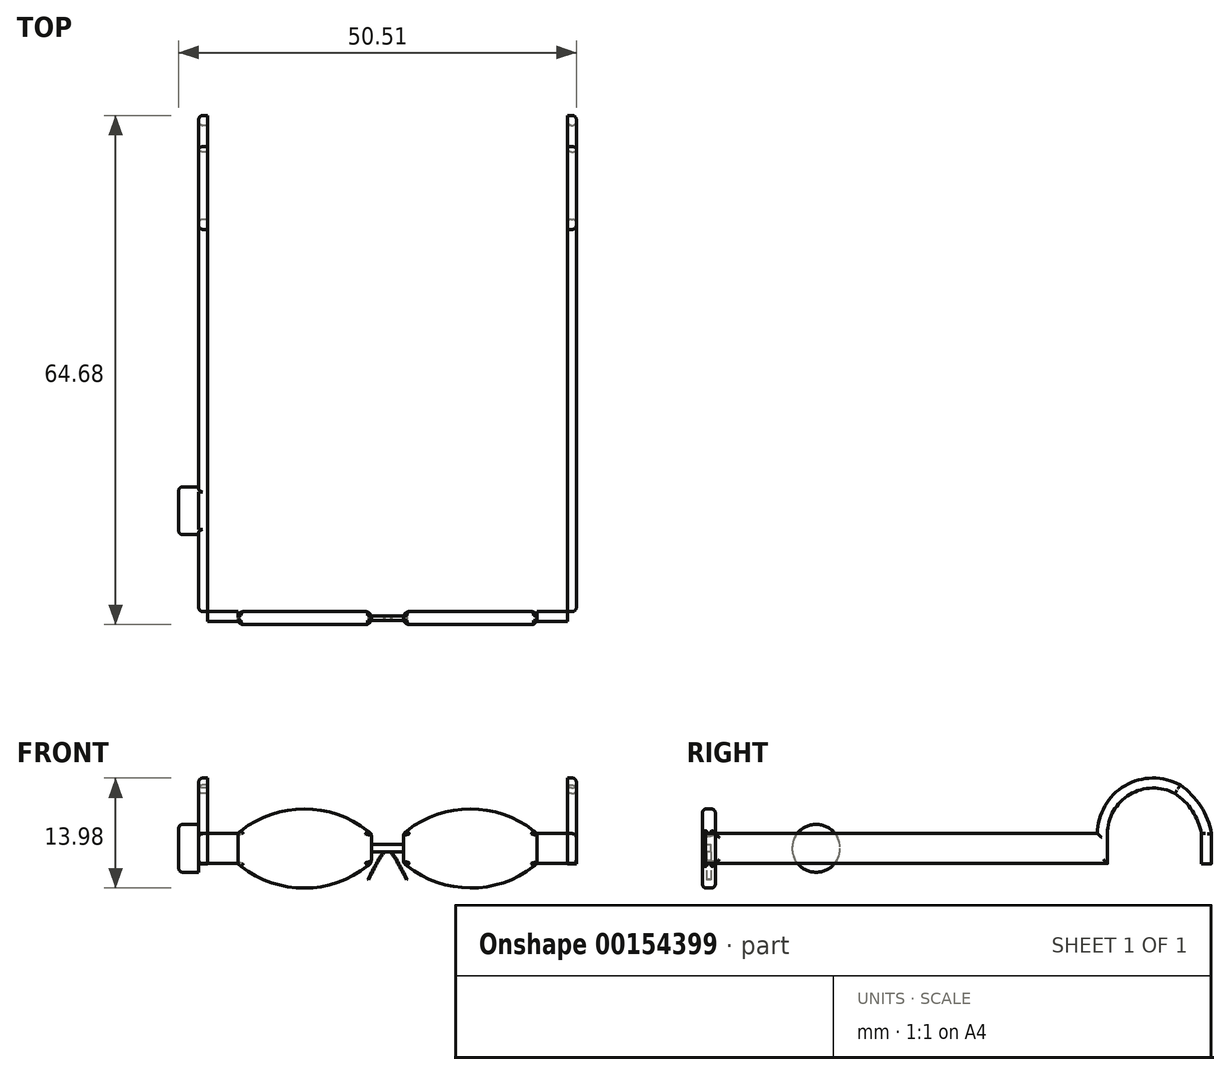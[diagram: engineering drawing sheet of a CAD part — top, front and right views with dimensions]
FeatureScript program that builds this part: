
annotation { "Feature Type Name" : "Feature", "Feature Type Description" : "" }
export const myFeature = defineFeature(function(context is Context, id is Id, definition is map)
    precondition{}
    {
        {
            var Q0;
            Q0=qCreatedBy(makeId("Right.planeOp"),FACE);
            var sketch = newSketch(context, id + "F0", { "sketchPlane" : qUnion([Q0])});
            skLineSegment(sketch, "E0.bottom", {"start": v(-42.94, 25.75) * mm, "end": v(5.61, 25.75) * mm});
            skLineSegment(sketch, "E0.top", {"start": v(-42.94, 21.94) * mm, "end": v(5.61, 21.94) * mm});
            skLineSegment(sketch, "E0.left", {"start": v(-42.94, 25.75) * mm, "end": v(-42.94, 21.94) * mm});
            skArc(sketch, "E1", {"start": v(16.12, 31.91) * mm, "mid": v(9.1, 31.84) * mm, "end": v(5.61, 25.75) * mm});
            skLineSegment(sketch, "E2", {"start": v(5.61, 21.94) * mm, "end": v(6.88, 21.94) * mm});
            skLineSegment(sketch, "E3", {"start": v(6.88, 21.94) * mm, "end": v(6.88, 25.75) * mm});
            skArc(sketch, "E4", {"start": v(15.45, 30.83) * mm, "mid": v(9.72, 30.73) * mm, "end": v(6.88, 25.75) * mm});
            skArc(sketch, "E5", {"start": v(20.09, 25.75) * mm, "mid": v(18.73, 29.23) * mm, "end": v(16.12, 31.91) * mm});
            skArc(sketch, "E6", {"start": v(18.82, 25.75) * mm, "mid": v(17.66, 28.64) * mm, "end": v(15.45, 30.83) * mm});
            skLineSegment(sketch, "E7", {"start": v(20.09, 25.75) * mm, "end": v(20.09, 21.93) * mm});
            skLineSegment(sketch, "E8", {"start": v(18.82, 25.75) * mm, "end": v(18.82, 21.94) * mm});
            skLineSegment(sketch, "E9", {"start": v(18.82, 21.94) * mm, "end": v(20.09, 21.93) * mm});
            skSolve(sketch);
        }
        {
            var Q0;
            Q0 = qSketchRegion(id + "F0", true);
            var Q1;
            Q1 = qConstructionFilter(qBodyType(qCreatedBy(id + "F0" ,EDGE), BodyType.WIRE), ConstructionObject.NO);
            extrude(context, id + "F1", {"entities" : qUnion([Q0]), "surfaceEntities" : qUnion([Q1]), "depth" : 1.14 * mm});
        }
        {
            var Q0;
            Q0=makeQuery(id+"F1.opExtrude","SWEPT_FACE",FACE,{"disambiguationData":[OSD([sQuery(id+"F0.wireOp",EDGE,"E0.left")])]});
            var sketch = newSketch(context, id + "F2", { "sketchPlane" : qUnion([Q0])});
            skLineSegment(sketch, "E10", {"start": v(4.93, 21.94) * mm, "end": v(4.93, 25.75) * mm});
            skLineSegment(sketch, "E11", {"start": v(21.93, 25.74) * mm, "end": v(21.93, 22) * mm});
            skLineSegment(sketch, "E12.MirrorCS", {"start": v(26, 25.75) * mm, "end": v(26, 22.02) * mm});
            skLineSegment(sketch, "E13.MirrorCS", {"start": v(43, 21.95) * mm, "end": v(43, 25.75) * mm});
            skLineSegment(sketch, "E14", {"start": v(46.79, 25.75) * mm, "end": v(46.79, 21.94) * mm});
            skLineSegment(sketch, "E15", {"start": v(1.14, 25.75) * mm, "end": v(1.14, 21.94) * mm});
            skArc(sketch, "E16", {"start": v(21.93, 25.74) * mm, "mid": v(13.43, 28.89) * mm, "end": v(4.93, 25.75) * mm});
            skArc(sketch, "E17", {"start": v(4.93, 21.94) * mm, "mid": v(13.44, 18.83) * mm, "end": v(21.93, 22) * mm});
            skArc(sketch, "E18", {"start": v(43, 25.75) * mm, "mid": v(34.5, 28.89) * mm, "end": v(26, 25.75) * mm});
            skArc(sketch, "E19", {"start": v(26, 22.02) * mm, "mid": v(34.5, 18.84) * mm, "end": v(43, 21.95) * mm});
            skLineSegment(sketch, "E20", {"start": v(4.93, 25.75) * mm, "end": v(1.14, 25.75) * mm});
            skLineSegment(sketch, "E21", {"start": v(43, 25.75) * mm, "end": v(46.79, 25.75) * mm});
            skLineSegment(sketch, "E22", {"start": v(26, 25.75) * mm, "end": v(43, 25.75) * mm});
            skLineSegment(sketch, "E23", {"start": v(21.93, 25.74) * mm, "end": v(4.93, 25.75) * mm});
            skLineSegment(sketch, "E24", {"start": v(26, 22.02) * mm, "end": v(43, 21.95) * mm});
            skSolve(sketch);
        }
        {
            var Q0;
            Q0 = qSketchRegion(id + "F2", true);
            extrude(context, id + "F3", {"entities" : qUnion([Q0]), "depth" : 1.65 * mm});
        }
        {
            var Q0;
            Q0=makeQuery(id+"F3.opExtrude","SWEPT_FACE",FACE,{"disambiguationData":[OSD([sQuery(id+"F2.wireOp",EDGE,"E12.MirrorCS")])]});
            var sketch = newSketch(context, id + "F4", { "sketchPlane" : qUnion([Q0])});
            skLineSegment(sketch, "E25.top", {"start": v(42.94, 25.75) * mm, "end": v(44.6, 25.75) * mm});
            skLineSegment(sketch, "E25.left", {"start": v(42.94, 25.75) * mm, "end": v(42.94, 25.75) * mm});
            skLineSegment(sketch, "E26.bottom", {"start": v(44.6, 22.02) * mm, "end": v(42.94, 22.02) * mm});
            skLineSegment(sketch, "E26.top", {"start": v(44.6, 25.75) * mm, "end": v(42.94, 25.75) * mm});
            skLineSegment(sketch, "E27", {"start": v(43.77, 25.75) * mm, "end": v(43.77, 22.02) * mm});
            skLineSegment(sketch, "E28", {"start": v(44.6, 23.88) * mm, "end": v(42.94, 23.88) * mm});
            skLineSegment(sketch, "E29.bottom", {"start": v(44.05, 23.4) * mm, "end": v(43.49, 23.4) * mm});
            skLineSegment(sketch, "E29.top", {"start": v(44.05, 24.36) * mm, "end": v(43.49, 24.36) * mm});
            skLineSegment(sketch, "E29.left", {"start": v(44.05, 23.4) * mm, "end": v(44.05, 24.36) * mm});
            skLineSegment(sketch, "E29.right", {"start": v(43.49, 23.4) * mm, "end": v(43.49, 24.36) * mm});
            skPoint(sketch, "E29.middle", {"position": v(43.77, 23.88) * mm});
            skSolve(sketch);
        }
        {
            var Q0;
            Q0 = qSketchRegion(id + "F4", true);
            extrude(context, id + "F5", {"entities" : qUnion([Q0]), "depth" : 4.13 * mm});
        }
        {
            var Q0;
            Q0=makeQuery(id+"F3.opExtrude","CAP_EDGE",EDGE,{"disambiguationData":[OSD([sQuery(id+"F2.wireOp",EDGE,"fc72fb57-17bc-4aef-a6e9-9f42b666f3fd4.MirrorCS")])],"isStart":false});
            var Q1;
            Q1=makeQuery(id+"F3.opExtrude","CAP_EDGE",EDGE,{"disambiguationData":[OSD([sQuery(id+"F2.wireOp",EDGE,"fc72fb57-17bc-4aef-a6e9-9f42b666f3fd4.MirrorCS")])],"isStart":true});
            var Q2;
            Q2=makeQuery(id+"F3.opExtrude","CAP_EDGE",EDGE,{"disambiguationData":[OSD([sQuery(id+"F2.wireOp",EDGE,"fc72fb57-17bc-4aef-a6e9-9f42b666f3fd3.MirrorCS")])],"isStart":false});
            var Q3;
            Q3=makeQuery(id+"F3.opExtrude","CAP_EDGE",EDGE,{"disambiguationData":[OSD([sQuery(id+"F2.wireOp",EDGE,"E12.MirrorCS")])],"isStart":false});
            var Q4;
            Q4=makeQuery(id+"F3.opExtrude","CAP_EDGE",EDGE,{"disambiguationData":[OSD([sQuery(id+"F2.wireOp",EDGE,"E12.MirrorCS")])],"isStart":true});
            var Q5;
            Q5=makeQuery(id+"F3.opExtrude","CAP_EDGE",EDGE,{"disambiguationData":[OSD([sQuery(id+"F2.wireOp",EDGE,"E13.MirrorCS")])],"isStart":false});
            var Q6;
            Q6=makeQuery(id+"F3.opExtrude","CAP_EDGE",EDGE,{"disambiguationData":[OSD([sQuery(id+"F2.wireOp",EDGE,"E13.MirrorCS")])],"isStart":true});
            var Q7;
            Q7=makeQuery(id+"F3.opExtrude","CAP_EDGE",EDGE,{"disambiguationData":[OSD([sQuery(id+"F2.wireOp",EDGE,"fc72fb57-17bc-4aef-a6e9-9f42b666f3fd3.MirrorCS")])],"isStart":true});
            var Q8;
            Q8=makeQuery(id+"F3.opExtrude","SWEPT_EDGE",EDGE,{"disambiguationData":[OSD([sQuery(id+"F2.wireOp",EDGE,"E12.MirrorCS"),sQuery(id+"F2.wireOp",EDGE,"fc72fb57-17bc-4aef-a6e9-9f42b666f3fd3.MirrorCS")])]});
            var Q9;
            Q9=makeQuery(id+"F3.opExtrude","SWEPT_EDGE",EDGE,{"disambiguationData":[OSD([sQuery(id+"F2.wireOp",EDGE,"E13.MirrorCS"),sQuery(id+"F2.wireOp",EDGE,"fc72fb57-17bc-4aef-a6e9-9f42b666f3fd3.MirrorCS")])]});
            var Q10;
            Q10=makeQuery(id+"F3.opExtrude","SWEPT_EDGE",EDGE,{"disambiguationData":[OSD([sQuery(id+"F2.wireOp",EDGE,"E13.MirrorCS"),sQuery(id+"F2.wireOp",EDGE,"fc72fb57-17bc-4aef-a6e9-9f42b666f3fd4.MirrorCS")])]});
            var Q11;
            Q11=makeQuery(id+"F3.opExtrude","CAP_EDGE",EDGE,{"disambiguationData":[OSD([sQuery(id+"F2.wireOp",EDGE,"E11")])],"isStart":true});
            var Q12;
            Q12=makeQuery(id+"F3.opExtrude","CAP_EDGE",EDGE,{"disambiguationData":[OSD([sQuery(id+"F2.wireOp",EDGE,"Gw3rG4JB-EbLj-57Wy-lnNk-VX72aqHDyFKe")])],"isStart":true});
            var Q13;
            Q13=makeQuery(id+"F3.opExtrude","CAP_EDGE",EDGE,{"disambiguationData":[OSD([sQuery(id+"F2.wireOp",EDGE,"E10")])],"isStart":true});
            var Q14;
            Q14=makeQuery(id+"F3.opExtrude","CAP_EDGE",EDGE,{"disambiguationData":[OSD([sQuery(id+"F2.wireOp",EDGE,"WBxUGhEL-5RnM-yJQJ-tIyO-uS8Gcnr4RgbC")])],"isStart":true});
            var Q15;
            Q15=makeQuery(id+"F3.opExtrude","CAP_EDGE",EDGE,{"disambiguationData":[OSD([sQuery(id+"F2.wireOp",EDGE,"Gw3rG4JB-EbLj-57Wy-lnNk-VX72aqHDyFKe")])],"isStart":false});
            var Q16;
            Q16=makeQuery(id+"F3.opExtrude","SWEPT_FACE",FACE,{"disambiguationData":[OSD([sQuery(id+"F2.wireOp",EDGE,"Gw3rG4JB-EbLj-57Wy-lnNk-VX72aqHDyFKe")])]});
            var Q17;
            Q17=makeQuery(id+"F3.opExtrude","CAP_EDGE",EDGE,{"disambiguationData":[OSD([sQuery(id+"F2.wireOp",EDGE,"E11")])],"isStart":false});
            var Q18;
            Q18=makeQuery(id+"F3.opExtrude","SWEPT_EDGE",EDGE,{"disambiguationData":[OSD([sQuery(id+"F2.wireOp",EDGE,"E11"),sQuery(id+"F2.wireOp",EDGE,"WBxUGhEL-5RnM-yJQJ-tIyO-uS8Gcnr4RgbC")])]});
            var Q19;
            Q19=makeQuery(id+"F3.opExtrude","CAP_EDGE",EDGE,{"disambiguationData":[OSD([sQuery(id+"F2.wireOp",EDGE,"E10")])],"isStart":false});
            var Q20;
            Q20=makeQuery(id+"F3.opExtrude","CAP_EDGE",EDGE,{"disambiguationData":[OSD([sQuery(id+"F2.wireOp",EDGE,"WBxUGhEL-5RnM-yJQJ-tIyO-uS8Gcnr4RgbC")])],"isStart":false});
            fillet(context, id + "F6", {"entities" : qUnion([Q0, Q1, Q2, Q3, Q4, Q5, Q6, Q7, Q8, Q9, Q10, Q11, Q12, Q13, Q14, Q15, Q16, Q17, Q18, Q19, Q20]), "radius" : 0.76 * mm, "tangentPropagation" : true, "allowEdgeOverflow" : false});
        }
        {
            var Q0;
            Q0=makeQuery(id+"F1.opExtrude","SWEPT_FACE",FACE,{"disambiguationData":[OSD([sQuery(id+"F0.wireOp",EDGE,"E0.left")])]});
            var sketch = newSketch(context, id + "F7", { "sketchPlane" : qUnion([Q0])});
            skLineSegment(sketch, "E30.bottom", {"start": v(1.14, 25.75) * mm, "end": v(5.01, 25.75) * mm});
            skLineSegment(sketch, "E30.top", {"start": v(1.14, 21.94) * mm, "end": v(5.01, 21.94) * mm});
            skLineSegment(sketch, "E30.left", {"start": v(1.14, 25.75) * mm, "end": v(1.14, 21.94) * mm});
            skLineSegment(sketch, "E30.right", {"start": v(5.01, 25.75) * mm, "end": v(5.01, 21.94) * mm});
            skSolve(sketch);
        }
        {
            var Q0;
            Q0=makeQuery(id+"F7.imprint","IMPRINT",FACE,{"disambiguationData":[TD([[makeQuery(id+"F7.imprint","IMPRINT",EDGE,{"derivedFrom":sQuery(id+"F7.wireOp",EDGE,"E30.bottom")}),-1.0]])]});
            extrude(context, id + "F8", {"entities" : qUnion([Q0]), "depth" : 1.27 * mm});
        }
        {
            var Q0;
            Q0=makeQuery(id+"F3.opExtrude","SWEPT_FACE",FACE,{"disambiguationData":[OSD([sQuery(id+"F2.wireOp",EDGE,"E11")])]});
            cPlane(context, id + "F9", {"entities" : qUnion([Q0]), "cplaneType" : CPlaneType.OFFSET, "offset" : 2.06 * mm, "width" : 152.4 * mm, "height" : 152.4 * mm});
        }
        {
            var Q0;
            Q0=makeQuery(id+"F1.opExtrude","SWEPT_BODY",BODY,{"disambiguationData":[OSD([sQuery(id+"F0.wireOp",EDGE,"E0.bottom"),sQuery(id+"F0.wireOp",EDGE,"E0.top"),sQuery(id+"F0.wireOp",EDGE,"E0.left"),sQuery(id+"F0.wireOp",EDGE,"E1"),sQuery(id+"F0.wireOp",EDGE,"E2"),sQuery(id+"F0.wireOp",EDGE,"E3"),sQuery(id+"F0.wireOp",EDGE,"E4"),sQuery(id+"F0.wireOp",EDGE,"E5"),sQuery(id+"F0.wireOp",EDGE,"E6"),sQuery(id+"F0.wireOp",EDGE,"E7"),sQuery(id+"F0.wireOp",EDGE,"E8"),sQuery(id+"F0.wireOp",EDGE,"E9")])]});
            var Q1;
            Q1=makeQuery(id+"F8.opExtrude","SWEPT_BODY",BODY,{"disambiguationData":[OSD([sQuery(id+"F7.wireOp",EDGE,"E30.bottom"),sQuery(id+"F7.wireOp",EDGE,"E30.top"),sQuery(id+"F7.wireOp",EDGE,"E30.left"),sQuery(id+"F7.wireOp",EDGE,"E30.right")])]});
            var Q2;
            Q2=qCreatedBy(id+"F9.planeOp",FACE);
            mirror(context, id + "F10", {"entities" : qUnion([Q0, Q1]), "mirrorPlane" : qUnion([Q2])});
        }
        {
            var Q0;
            Q0=makeQuery(id+"F1.opExtrude","CAP_FACE",FACE,{"disambiguationData":[OSD([sQuery(id+"F0.wireOp",EDGE,"E0.bottom"),sQuery(id+"F0.wireOp",EDGE,"E0.top"),sQuery(id+"F0.wireOp",EDGE,"E0.left"),sQuery(id+"F0.wireOp",EDGE,"E1"),sQuery(id+"F0.wireOp",EDGE,"E2"),sQuery(id+"F0.wireOp",EDGE,"E3"),sQuery(id+"F0.wireOp",EDGE,"E4"),sQuery(id+"F0.wireOp",EDGE,"E5"),sQuery(id+"F0.wireOp",EDGE,"E6"),sQuery(id+"F0.wireOp",EDGE,"E7"),sQuery(id+"F0.wireOp",EDGE,"E8"),sQuery(id+"F0.wireOp",EDGE,"E9")])],"isStart":true});
            var sketch = newSketch(context, id + "F11", { "sketchPlane" : qUnion([Q0])});
            skCircle(sketch, "E31", {"center": v(30.13, 23.89) * mm, "radius": 3.04 * mm});
            skSolve(sketch);
        }
        {
            var Q0;
            {var subQ0=sQuery(id+"F11.wireOp",EDGE,"E31");var subQ1=makeQuery(id+"F1.opExtrude","CAP_EDGE",EDGE,{"disambiguationData":[OSD([sQuery(id+"F0.wireOp",EDGE,"E0.top"),sQuery(id+"F0.wireOp",EDGE,"E2")])],"isStart":true});var subQ2=makeQuery(id+"F11.imprint","INTERSECT",VERTEX,{"disambiguationData":[OD(0.0)],"derivedFrom":[subQ1,subQ0]});Q0=makeQuery(id+"F11.imprint","IMPRINT",FACE,{"disambiguationData":[TD([[makeQuery(id+"F11.imprint","IMPRINT",EDGE,{"disambiguationData":[TD([[subQ2,-1.0]])],"derivedFrom":subQ0}),1.0]])]});}
            var Q1;
            {var subQ0=sQuery(id+"F11.wireOp",EDGE,"E31");var subQ1=makeQuery(id+"F1.opExtrude","CAP_EDGE",EDGE,{"disambiguationData":[OSD([sQuery(id+"F0.wireOp",EDGE,"E0.bottom")])],"isStart":true});var subQ2=makeQuery(id+"F11.imprint","INTERSECT",VERTEX,{"disambiguationData":[OD(0.0)],"derivedFrom":[subQ1,subQ0]});Q1=makeQuery(id+"F11.imprint","IMPRINT",FACE,{"disambiguationData":[TD([[makeQuery(id+"F11.imprint","IMPRINT",EDGE,{"disambiguationData":[TD([[subQ2,1.0]])],"derivedFrom":subQ1}),1.0]])]});}
            var Q2;
            {var subQ0=sQuery(id+"F11.wireOp",EDGE,"E31");var subQ1=makeQuery(id+"F1.opExtrude","CAP_EDGE",EDGE,{"disambiguationData":[OSD([sQuery(id+"F0.wireOp",EDGE,"E0.bottom")])],"isStart":true});var subQ2=makeQuery(id+"F11.imprint","INTERSECT",VERTEX,{"disambiguationData":[OD(0.0)],"derivedFrom":[subQ1,subQ0]});Q2=makeQuery(id+"F11.imprint","IMPRINT",FACE,{"disambiguationData":[TD([[makeQuery(id+"F11.imprint","IMPRINT",EDGE,{"disambiguationData":[TD([[subQ2,1.0]])],"derivedFrom":subQ0}),1.0]])]});}
            extrude(context, id + "F12", {"entities" : qUnion([Q0, Q1, Q2]), "operationType" : NewBodyOperationType.ADD, "depth" : 2.54 * mm});
        }
        {
            var Q0;
            Q0=makeQuery(id+"F12.opExtrude","CAP_EDGE",EDGE,{"disambiguationData":[OSD([sQuery(id+"F11.wireOp",EDGE,"E31")])],"isStart":false});
            var Q1;
            {var subQ0=sQuery(id+"F11.wireOp",EDGE,"E31");var subQ1=sQuery(id+"F0.wireOp",EDGE,"E1");var subQ2=sQuery(id+"F0.wireOp",EDGE,"E0.bottom");Q1=makeQuery(id+"F12.boolean.opBoolean","SPLIT",EDGE,{"disambiguationData":[TD([makeQuery(id+"F1.opExtrude","SWEPT_FACE",FACE,{"disambiguationData":[OSD([subQ2])]}),makeQuery(id+"F1.opExtrude","CAP_FACE",FACE,{"disambiguationData":[OSD([subQ2,sQuery(id+"F0.wireOp",EDGE,"E0.top"),sQuery(id+"F0.wireOp",EDGE,"E0.left"),subQ1,sQuery(id+"F0.wireOp",EDGE,"E2"),sQuery(id+"F0.wireOp",EDGE,"E3"),sQuery(id+"F0.wireOp",EDGE,"E4"),sQuery(id+"F0.wireOp",EDGE,"E5"),sQuery(id+"F0.wireOp",EDGE,"E6"),sQuery(id+"F0.wireOp",EDGE,"E7"),sQuery(id+"F0.wireOp",EDGE,"E8"),sQuery(id+"F0.wireOp",EDGE,"E9")])],"isStart":true}),makeQuery(id+"F1.opExtrude","SWEPT_FACE",FACE,{"disambiguationData":[OSD([subQ1])]}),makeQuery(id+"F12.opExtrude","SWEPT_FACE",FACE,{"disambiguationData":[OSD([subQ0])]}),makeQuery(id+"F12.opExtrude","CAP_FACE",FACE,{"disambiguationData":[OSD([subQ0])],"isStart":true})])],"derivedFrom":makeQuery(id+"F1.opExtrude","CAP_EDGE",EDGE,{"disambiguationData":[OSD([subQ2])],"isStart":true})});}
            var Q2;
            {var subQ0=sQuery(id+"F11.wireOp",EDGE,"E31");var subQ1=sQuery(id+"F0.wireOp",EDGE,"E0.left");var subQ2=sQuery(id+"F0.wireOp",EDGE,"E0.bottom");Q2=makeQuery(id+"F12.boolean.opBoolean","SPLIT",EDGE,{"disambiguationData":[TD([makeQuery(id+"F1.opExtrude","SWEPT_FACE",FACE,{"disambiguationData":[OSD([subQ2])]}),makeQuery(id+"F1.opExtrude","CAP_FACE",FACE,{"disambiguationData":[OSD([subQ2,sQuery(id+"F0.wireOp",EDGE,"E0.top"),subQ1,sQuery(id+"F0.wireOp",EDGE,"E1"),sQuery(id+"F0.wireOp",EDGE,"E2"),sQuery(id+"F0.wireOp",EDGE,"E3"),sQuery(id+"F0.wireOp",EDGE,"E4"),sQuery(id+"F0.wireOp",EDGE,"E5"),sQuery(id+"F0.wireOp",EDGE,"E6"),sQuery(id+"F0.wireOp",EDGE,"E7"),sQuery(id+"F0.wireOp",EDGE,"E8"),sQuery(id+"F0.wireOp",EDGE,"E9")])],"isStart":true}),makeQuery(id+"F1.opExtrude","SWEPT_FACE",FACE,{"disambiguationData":[OSD([subQ1])]}),makeQuery(id+"F12.opExtrude","SWEPT_FACE",FACE,{"disambiguationData":[OSD([subQ0])]}),makeQuery(id+"F12.opExtrude","CAP_FACE",FACE,{"disambiguationData":[OSD([subQ0])],"isStart":true})])],"derivedFrom":makeQuery(id+"F1.opExtrude","CAP_EDGE",EDGE,{"disambiguationData":[OSD([subQ2])],"isStart":true})});}
            var Q3;
            Q3=makeQuery(id+"F1.opExtrude","CAP_EDGE",EDGE,{"disambiguationData":[OSD([sQuery(id+"F0.wireOp",EDGE,"E0.left")])],"isStart":true});
            var Q4;
            {var subQ0=sQuery(id+"F0.wireOp",EDGE,"E3");var subQ1=sQuery(id+"F11.wireOp",EDGE,"E31");var subQ2=sQuery(id+"F0.wireOp",EDGE,"E2");var subQ3=sQuery(id+"F0.wireOp",EDGE,"E0.top");Q4=makeQuery(id+"F12.boolean.opBoolean","SPLIT",EDGE,{"disambiguationData":[TD([makeQuery(id+"F1.opExtrude","CAP_FACE",FACE,{"disambiguationData":[OSD([sQuery(id+"F0.wireOp",EDGE,"E0.bottom"),subQ3,sQuery(id+"F0.wireOp",EDGE,"E0.left"),sQuery(id+"F0.wireOp",EDGE,"E1"),subQ2,subQ0,sQuery(id+"F0.wireOp",EDGE,"E4"),sQuery(id+"F0.wireOp",EDGE,"E5"),sQuery(id+"F0.wireOp",EDGE,"E6"),sQuery(id+"F0.wireOp",EDGE,"E7"),sQuery(id+"F0.wireOp",EDGE,"E8"),sQuery(id+"F0.wireOp",EDGE,"E9")])],"isStart":true}),makeQuery(id+"F1.opExtrude","SWEPT_FACE",FACE,{"disambiguationData":[OSD([subQ3,subQ2])]}),makeQuery(id+"F1.opExtrude","SWEPT_FACE",FACE,{"disambiguationData":[OSD([subQ0])]}),makeQuery(id+"F12.opExtrude","SWEPT_FACE",FACE,{"disambiguationData":[OSD([subQ1])]}),makeQuery(id+"F12.opExtrude","CAP_FACE",FACE,{"disambiguationData":[OSD([subQ1])],"isStart":true})])],"derivedFrom":makeQuery(id+"F1.opExtrude","CAP_EDGE",EDGE,{"disambiguationData":[OSD([subQ3,subQ2])],"isStart":true})});}
            var Q5;
            {var subQ0=sQuery(id+"F0.wireOp",EDGE,"E0.left");var subQ1=sQuery(id+"F11.wireOp",EDGE,"E31");var subQ2=sQuery(id+"F0.wireOp",EDGE,"E2");var subQ3=sQuery(id+"F0.wireOp",EDGE,"E0.top");Q5=makeQuery(id+"F12.boolean.opBoolean","SPLIT",EDGE,{"disambiguationData":[TD([makeQuery(id+"F1.opExtrude","CAP_FACE",FACE,{"disambiguationData":[OSD([sQuery(id+"F0.wireOp",EDGE,"E0.bottom"),subQ3,subQ0,sQuery(id+"F0.wireOp",EDGE,"E1"),subQ2,sQuery(id+"F0.wireOp",EDGE,"E3"),sQuery(id+"F0.wireOp",EDGE,"E4"),sQuery(id+"F0.wireOp",EDGE,"E5"),sQuery(id+"F0.wireOp",EDGE,"E6"),sQuery(id+"F0.wireOp",EDGE,"E7"),sQuery(id+"F0.wireOp",EDGE,"E8"),sQuery(id+"F0.wireOp",EDGE,"E9")])],"isStart":true}),makeQuery(id+"F1.opExtrude","SWEPT_FACE",FACE,{"disambiguationData":[OSD([subQ3,subQ2])]}),makeQuery(id+"F1.opExtrude","SWEPT_FACE",FACE,{"disambiguationData":[OSD([subQ0])]}),makeQuery(id+"F12.opExtrude","SWEPT_FACE",FACE,{"disambiguationData":[OSD([subQ1])]}),makeQuery(id+"F12.opExtrude","CAP_FACE",FACE,{"disambiguationData":[OSD([subQ1])],"isStart":true})])],"derivedFrom":makeQuery(id+"F1.opExtrude","CAP_EDGE",EDGE,{"disambiguationData":[OSD([subQ3,subQ2])],"isStart":true})});}
            var Q6;
            Q6=makeQuery(id+"F1.opExtrude","CAP_EDGE",EDGE,{"disambiguationData":[OSD([sQuery(id+"F0.wireOp",EDGE,"E3")])],"isStart":true});
            var Q7;
            Q7=makeQuery(id+"F1.opExtrude","CAP_EDGE",EDGE,{"disambiguationData":[OSD([sQuery(id+"F0.wireOp",EDGE,"E6")])],"isStart":true});
            var Q8;
            Q8=makeQuery(id+"F1.opExtrude","CAP_EDGE",EDGE,{"disambiguationData":[OSD([sQuery(id+"F0.wireOp",EDGE,"E8")])],"isStart":true});
            var Q9;
            Q9=makeQuery(id+"F1.opExtrude","CAP_EDGE",EDGE,{"disambiguationData":[OSD([sQuery(id+"F0.wireOp",EDGE,"E7")])],"isStart":true});
            var Q10;
            Q10=makeQuery(id+"F1.opExtrude","CAP_EDGE",EDGE,{"disambiguationData":[OSD([sQuery(id+"F0.wireOp",EDGE,"E5")])],"isStart":true});
            var Q11;
            Q11=makeQuery(id+"F1.opExtrude","CAP_EDGE",EDGE,{"disambiguationData":[OSD([sQuery(id+"F0.wireOp",EDGE,"E1")])],"isStart":true});
            var Q12;
            Q12=makeQuery(id+"F1.opExtrude","CAP_EDGE",EDGE,{"disambiguationData":[OSD([sQuery(id+"F0.wireOp",EDGE,"E4")])],"isStart":true});
            var Q13;
            Q13=makeQuery(id+"F10.opPattern","COPY",EDGE,{"derivedFrom":makeQuery(id+"F1.opExtrude","CAP_EDGE",EDGE,{"disambiguationData":[OSD([sQuery(id+"F0.wireOp",EDGE,"E0.bottom")])],"isStart":true}),"instanceName":"1"});
            var Q14;
            Q14=makeQuery(id+"F10.opPattern","COPY",EDGE,{"derivedFrom":makeQuery(id+"F1.opExtrude","CAP_EDGE",EDGE,{"disambiguationData":[OSD([sQuery(id+"F0.wireOp",EDGE,"E0.top"),sQuery(id+"F0.wireOp",EDGE,"E2")])],"isStart":true}),"instanceName":"1"});
            var Q15;
            Q15=makeQuery(id+"F10.opPattern","COPY",EDGE,{"derivedFrom":makeQuery(id+"F1.opExtrude","CAP_EDGE",EDGE,{"disambiguationData":[OSD([sQuery(id+"F0.wireOp",EDGE,"E0.left")])],"isStart":true}),"instanceName":"1"});
            var Q16;
            Q16=makeQuery(id+"F10.opPattern","COPY",EDGE,{"derivedFrom":makeQuery(id+"F1.opExtrude","CAP_EDGE",EDGE,{"disambiguationData":[OSD([sQuery(id+"F0.wireOp",EDGE,"E3")])],"isStart":true}),"instanceName":"1"});
            var Q17;
            Q17=makeQuery(id+"F10.opPattern","COPY",EDGE,{"derivedFrom":makeQuery(id+"F1.opExtrude","CAP_EDGE",EDGE,{"disambiguationData":[OSD([sQuery(id+"F0.wireOp",EDGE,"E6")])],"isStart":true}),"instanceName":"1"});
            var Q18;
            Q18=makeQuery(id+"F10.opPattern","COPY",EDGE,{"derivedFrom":makeQuery(id+"F1.opExtrude","CAP_EDGE",EDGE,{"disambiguationData":[OSD([sQuery(id+"F0.wireOp",EDGE,"E6")])],"isStart":false}),"instanceName":"1"});
            var Q19;
            Q19=makeQuery(id+"F10.opPattern","COPY",EDGE,{"derivedFrom":makeQuery(id+"F1.opExtrude","CAP_EDGE",EDGE,{"disambiguationData":[OSD([sQuery(id+"F0.wireOp",EDGE,"E8")])],"isStart":true}),"instanceName":"1"});
            var Q20;
            Q20=makeQuery(id+"F10.opPattern","COPY",EDGE,{"derivedFrom":makeQuery(id+"F1.opExtrude","CAP_EDGE",EDGE,{"disambiguationData":[OSD([sQuery(id+"F0.wireOp",EDGE,"E7")])],"isStart":true}),"instanceName":"1"});
            var Q21;
            Q21=makeQuery(id+"F10.opPattern","COPY",EDGE,{"derivedFrom":makeQuery(id+"F1.opExtrude","CAP_EDGE",EDGE,{"disambiguationData":[OSD([sQuery(id+"F0.wireOp",EDGE,"E5")])],"isStart":true}),"instanceName":"1"});
            var Q22;
            Q22=makeQuery(id+"F10.opPattern","COPY",EDGE,{"derivedFrom":makeQuery(id+"F1.opExtrude","CAP_EDGE",EDGE,{"disambiguationData":[OSD([sQuery(id+"F0.wireOp",EDGE,"E1")])],"isStart":true}),"instanceName":"1"});
            var Q23;
            Q23=makeQuery(id+"F10.opPattern","COPY",EDGE,{"derivedFrom":makeQuery(id+"F1.opExtrude","CAP_EDGE",EDGE,{"disambiguationData":[OSD([sQuery(id+"F0.wireOp",EDGE,"E8")])],"isStart":false}),"instanceName":"1"});
            var Q24;
            Q24=makeQuery(id+"F10.opPattern","COPY",EDGE,{"derivedFrom":makeQuery(id+"F1.opExtrude","CAP_EDGE",EDGE,{"disambiguationData":[OSD([sQuery(id+"F0.wireOp",EDGE,"E4")])],"isStart":false}),"instanceName":"1"});
            fillet(context, id + "F13", {"entities" : qUnion([Q0, Q1, Q2, Q3, Q4, Q5, Q6, Q7, Q8, Q9, Q10, Q11, Q12, Q13, Q14, Q15, Q16, Q17, Q18, Q19, Q20, Q21, Q22, Q23, Q24]), "radius" : 0.5 * mm, "tangentPropagation" : true, "allowEdgeOverflow" : false});
        }
        {
            var Q0;
            Q0=makeQuery(id+"F3.opExtrude","CAP_EDGE",EDGE,{"disambiguationData":[OSD([sQuery(id+"F2.wireOp",EDGE,"E16")])],"isStart":false});
            var Q1;
            Q1=makeQuery(id+"F3.opExtrude","CAP_EDGE",EDGE,{"disambiguationData":[OSD([sQuery(id+"F2.wireOp",EDGE,"E16")])],"isStart":true});
            var Q2;
            Q2=makeQuery(id+"F3.opExtrude","CAP_EDGE",EDGE,{"disambiguationData":[OSD([sQuery(id+"F2.wireOp",EDGE,"E17")])],"isStart":false});
            var Q3;
            Q3=makeQuery(id+"F3.opExtrude","CAP_EDGE",EDGE,{"disambiguationData":[OSD([sQuery(id+"F2.wireOp",EDGE,"E18")])],"isStart":true});
            var Q4;
            Q4=makeQuery(id+"F3.opExtrude","CAP_EDGE",EDGE,{"disambiguationData":[OSD([sQuery(id+"F2.wireOp",EDGE,"E18")])],"isStart":false});
            var Q5;
            Q5=makeQuery(id+"F3.opExtrude","CAP_EDGE",EDGE,{"disambiguationData":[OSD([sQuery(id+"F2.wireOp",EDGE,"E19")])],"isStart":false});
            var Q6;
            Q6=makeQuery(id+"F3.opExtrude","CAP_EDGE",EDGE,{"disambiguationData":[OSD([sQuery(id+"F2.wireOp",EDGE,"E19")])],"isStart":true});
            fillet(context, id + "F14", {"entities" : qUnion([Q0, Q1, Q2, Q3, Q4, Q5, Q6]), "radius" : 0.5 * mm, "tangentPropagation" : true, "allowEdgeOverflow" : false});
        }
        {
            var Q0;
            Q0=makeQuery(id+"F5.opExtrude","SWEPT_FACE",FACE,{"disambiguationData":[OSD([sQuery(id+"F4.wireOp",EDGE,"E29.left")])]});
            var sketch = newSketch(context, id + "F15", { "sketchPlane" : qUnion([Q0])});
            skLineSegment(sketch, "E32.bottom", {"start": v(26, 23.4) * mm, "end": v(21.88, 23.4) * mm});
            skLineSegment(sketch, "E32.top", {"start": v(26, 23.4) * mm, "end": v(21.88, 23.4) * mm});
            skLineSegment(sketch, "E32.left", {"start": v(26, 23.4) * mm, "end": v(26, 23.4) * mm});
            skLineSegment(sketch, "E32.right", {"start": v(21.88, 23.4) * mm, "end": v(21.88, 23.4) * mm});
            skFitSpline(sketch, "E33", {"points": [v(23.58, 23.4) * mm, v(22.96, 22.48) * mm, v(21.58, 19.9) * mm], "startDerivative": vector(-1.51, -2.1) * mm, "endDerivative": vector(-2.43, -4.71) * mm});
            skFitSpline(sketch, "E34", {"points": [v(23.45, 23.4) * mm, v(22.87, 22.53) * mm, v(21.98, 20.89) * mm, v(21.5, 19.94) * mm], "startDerivative": vector(-1.83, -2.58) * mm, "endDerivative": vector(-1.43, -2.85) * mm});
            skLineSegment(sketch, "E35", {"start": v(21.5, 19.94) * mm, "end": v(21.58, 19.9) * mm});
            skSolve(sketch);
        }
        {
            var Q0;
            Q0 = qSketchRegion(id + "F15", true);
            var Q1;
            Q1=makeQuery(id+"F5.opExtrude","SWEPT_FACE",FACE,{"disambiguationData":[OSD([sQuery(id+"F4.wireOp",EDGE,"E29.right")])]});
            extrude(context, id + "F16", {"entities" : qUnion([Q0]), "operationType" : NewBodyOperationType.ADD, "endBound" : BoundingType.UP_TO_SURFACE, "oppositeDirection" : true, "endBoundEntityFace" : qUnion([Q1]), "depth" : 25.4 * mm});
        }
        {
            var Q0;
            Q0=makeQuery(id+"F5.opExtrude","SWEPT_BODY",BODY,{"disambiguationData":[OSD([sQuery(id+"F4.wireOp",EDGE,"E29.bottom"),sQuery(id+"F4.wireOp",EDGE,"E29.top"),sQuery(id+"F4.wireOp",EDGE,"E29.left"),sQuery(id+"F4.wireOp",EDGE,"E29.right")])]});
            var Q1;
            Q1=qCreatedBy(id+"F9.planeOp",FACE);
            mirror(context, id + "F17", {"entities" : qUnion([Q0]), "mirrorPlane" : qUnion([Q1])});
        }
    });
